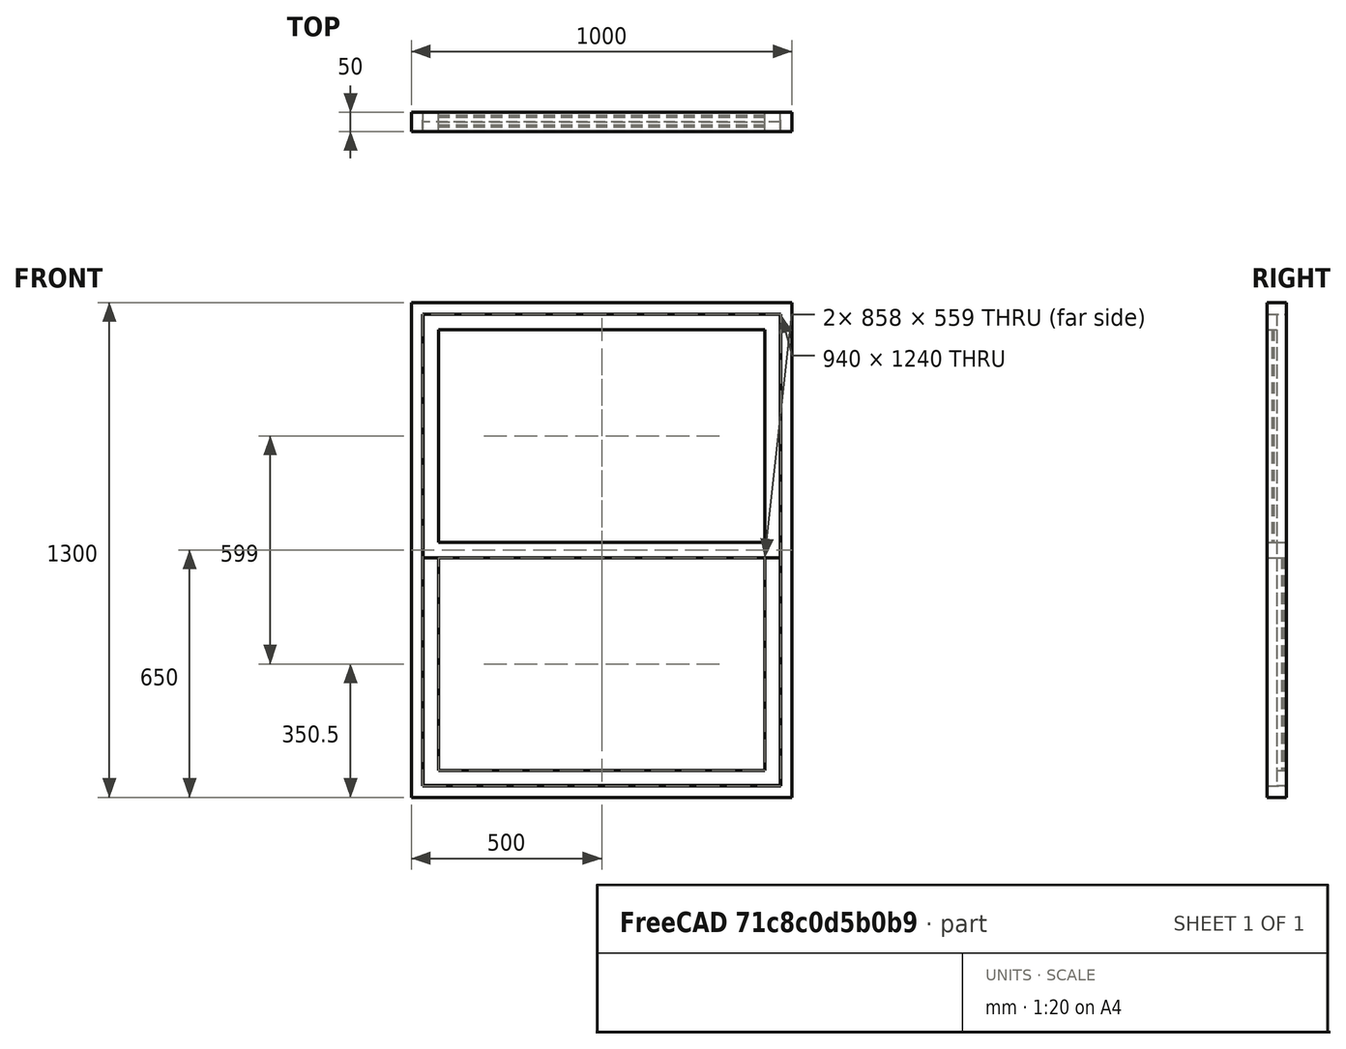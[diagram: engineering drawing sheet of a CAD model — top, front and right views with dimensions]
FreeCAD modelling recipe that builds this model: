
FCSTD DOCUMENT  (FreeCAD 0.16R6704 (Git))
Label: Sash window
License: CreativeCommons Attribution
LicenseURL: http://creativecommons.org/licenses/by/4.0/
objects: Sketcher::SketchObject×1, Part::FeaturePython×1
note: 2 computed .brp shape members not serialized (recipe doc carries the construction recipe); baked Part::Feature solids carry a one-line shape summary decoded from their .brp

FEATURE [Sketcher::SketchObject] Sketch090
  Placement = pos=(0,0,0) rot=(1,0,0;1.5708rad)
  sketch-geometry (24):
    g0: LineSegment StartX=0 StartY=1300 StartZ=0 EndX=0 EndY=0 EndZ=0
    g1: LineSegment StartX=0 StartY=0 StartZ=0 EndX=1000 EndY=0 EndZ=0
    g2: LineSegment StartX=1000 StartY=0 StartZ=0 EndX=1000 EndY=1300 EndZ=0
    g3: LineSegment StartX=1000 StartY=1300 StartZ=0 EndX=0 EndY=1300 EndZ=0
    g4: LineSegment StartX=71 StartY=1229 StartZ=0 EndX=71 EndY=670 EndZ=0
    g5: LineSegment StartX=71 StartY=670 StartZ=0 EndX=929 EndY=670 EndZ=0
    g6: LineSegment StartX=929 StartY=670 StartZ=0 EndX=929 EndY=1229 EndZ=0
    g7: LineSegment StartX=929 StartY=1229 StartZ=0 EndX=71 EndY=1229 EndZ=0
    g8: LineSegment StartX=31 StartY=670 StartZ=0 EndX=31 EndY=31 EndZ=0
    g9: LineSegment StartX=31 StartY=31 StartZ=0 EndX=969 EndY=31 EndZ=0
    g10: LineSegment StartX=969 StartY=31 StartZ=0 EndX=969 EndY=670 EndZ=0
    g11: LineSegment StartX=969 StartY=670 StartZ=0 EndX=31 EndY=670 EndZ=0
    g12: LineSegment StartX=71 StartY=630 StartZ=0 EndX=71 EndY=71 EndZ=0
    g13: LineSegment StartX=71 StartY=71 StartZ=0 EndX=929 EndY=71 EndZ=0
    g14: LineSegment StartX=929 StartY=71 StartZ=0 EndX=929 EndY=630 EndZ=0
    g15: LineSegment StartX=929 StartY=630 StartZ=0 EndX=71 EndY=630 EndZ=0
    g16: LineSegment StartX=30 StartY=1270 StartZ=0 EndX=30 EndY=30 EndZ=0
    g17: LineSegment StartX=30 StartY=30 StartZ=0 EndX=970 EndY=30 EndZ=0
    g18: LineSegment StartX=970 StartY=30 StartZ=0 EndX=970 EndY=1270 EndZ=0
    g19: LineSegment StartX=970 StartY=1270 StartZ=0 EndX=30 EndY=1270 EndZ=0
    g20: LineSegment StartX=31 StartY=1269 StartZ=0 EndX=31 EndY=630 EndZ=0
    g21: LineSegment StartX=31 StartY=630 StartZ=0 EndX=969 EndY=630 EndZ=0
    g22: LineSegment StartX=969 StartY=630 StartZ=0 EndX=969 EndY=1269 EndZ=0
    g23: LineSegment StartX=969 StartY=1269 StartZ=0 EndX=31 EndY=1269 EndZ=0
  constraints (71):
    c: Coincident(g0,g1)
    c: Coincident(g1,g2)
    c: Coincident(g2,g3)
    c: Vertical(g2)
    c: Coincident(g3,g0)
    c: Coincident(g4,g5)
    c: Vertical(g4)
    c: Coincident(g5,g6)
    c: Horizontal(g5)
    c: Coincident(g6,g7)
    c: Vertical(g6)
    c: Coincident(g7,g4)
    c: Coincident(g8,g9)
    c: Coincident(g9,g10)
    c: Coincident(g10,g11)
    c: Vertical(g10)
    c: Coincident(g11,g8)
    c: Coincident(g12,g13)
    c: Vertical(g12)
    c: Coincident(g13,g14)
    c: Coincident(g14,g15)
    c: Vertical(g14)
    c: Coincident(g15,g12)
    c: Coincident(g16,g17)
    c: Coincident(g17,g18)
    c: Coincident(g18,g19)
    c: Vertical(g18)
    c: Coincident(g19,g16)
    c: Coincident(g20,g21)
    c: Coincident(g21,g22)
    c: Coincident(g22,g23)
    c: Vertical(g22)
    c: Coincident(g23,g20)
    c: DistanceX(g16,g20) = 1
    c: DistanceX(g0,g16) = 30  'Largura perfil vertical 1'
    c: DistanceX(g20,g4) = 40  'Largura perfil vertical 1 janela'
    c: DistanceX(g6,g22) = 40  'Largura perfil vertical 2 janela'
    c: DistanceX(g22,g18) = 1
    c: DistanceX(g18,g2) = 30  'Largura vertical 2'
    c: DistanceY(g18,g2) = 30  'Altura perfil superior'
    c: DistanceY(g22,g18) = 1
    c: DistanceY(g6,g22) = 40  'Altura perfil superior janela'
    c: DistanceY(g20,g8) = 40  'Altura perfil inferior janela'
    c: DistanceY(g8,g12) = 40  'Altura perfil inferior 2'
    c: DistanceY(g16,g8) = 1
    c: DistanceY(g-1,g16) = 30  'Altura perfil inferior'
    c: Horizontal(g3)
    c: Horizontal(g19)
    c: Horizontal(g23)
    c: Horizontal(g7)
    c: Horizontal(g13)
    c: Horizontal(g9)
    c: Horizontal(g17)
    c: Horizontal(g1)
    c: Vertical(g0)
    c: Vertical(g16)
    c: Vertical(g20)
    c: Vertical(g8)
    c: Coincident(g0,g-1)
    c: DistanceX(g16,g8) = 1
    c: Horizontal(g11)
    c: Horizontal(g21)
    c: Horizontal(g15)
    c: DistanceY(g12,g20) = 0
    c: DistanceY(g4,g8) = 0
    c: DistanceX(g9,g17) = 1
    c: DistanceX(g0,g2) = 1000  'Largura do vão'
    c: DistanceY(g1,g2) = 1300  'Altura do vão'
    c: Equal(g6,g14)  'Constraint70'
    c: DistanceX(g4,g12) = 0
    c: DistanceX(g5,g14) = 0
FEATURE [Part::FeaturePython] Window070  label="Sash window"  # WARN: FeaturePython — macro-defined, semantics opaque (R4)
  Base = -> Sketch090
  Height = 0
  HoleDepth = 0
  MoveWithHost = true
  Normal = (0,1,0)
  Preset = 0
  Role = 0
  Width = 0
  WindowParts = MONTANTES | Frame | Wire0,Wire4 | 50.0 | 0.0 | MONTANTE SUPERIOR | Frame | Wire5,Wire1 | 25.0 | 0.0 | VIDRO SUPERIOR | Glass panel | Wire1 | 5.0 | 12.5 | MONTANTE INFERIOR | Frame | Wire2,Wire3 | 25.0 | 25.0 | VIDRO INFERIOR | Glass panel | Wire3 | 5.0 | 37.5
